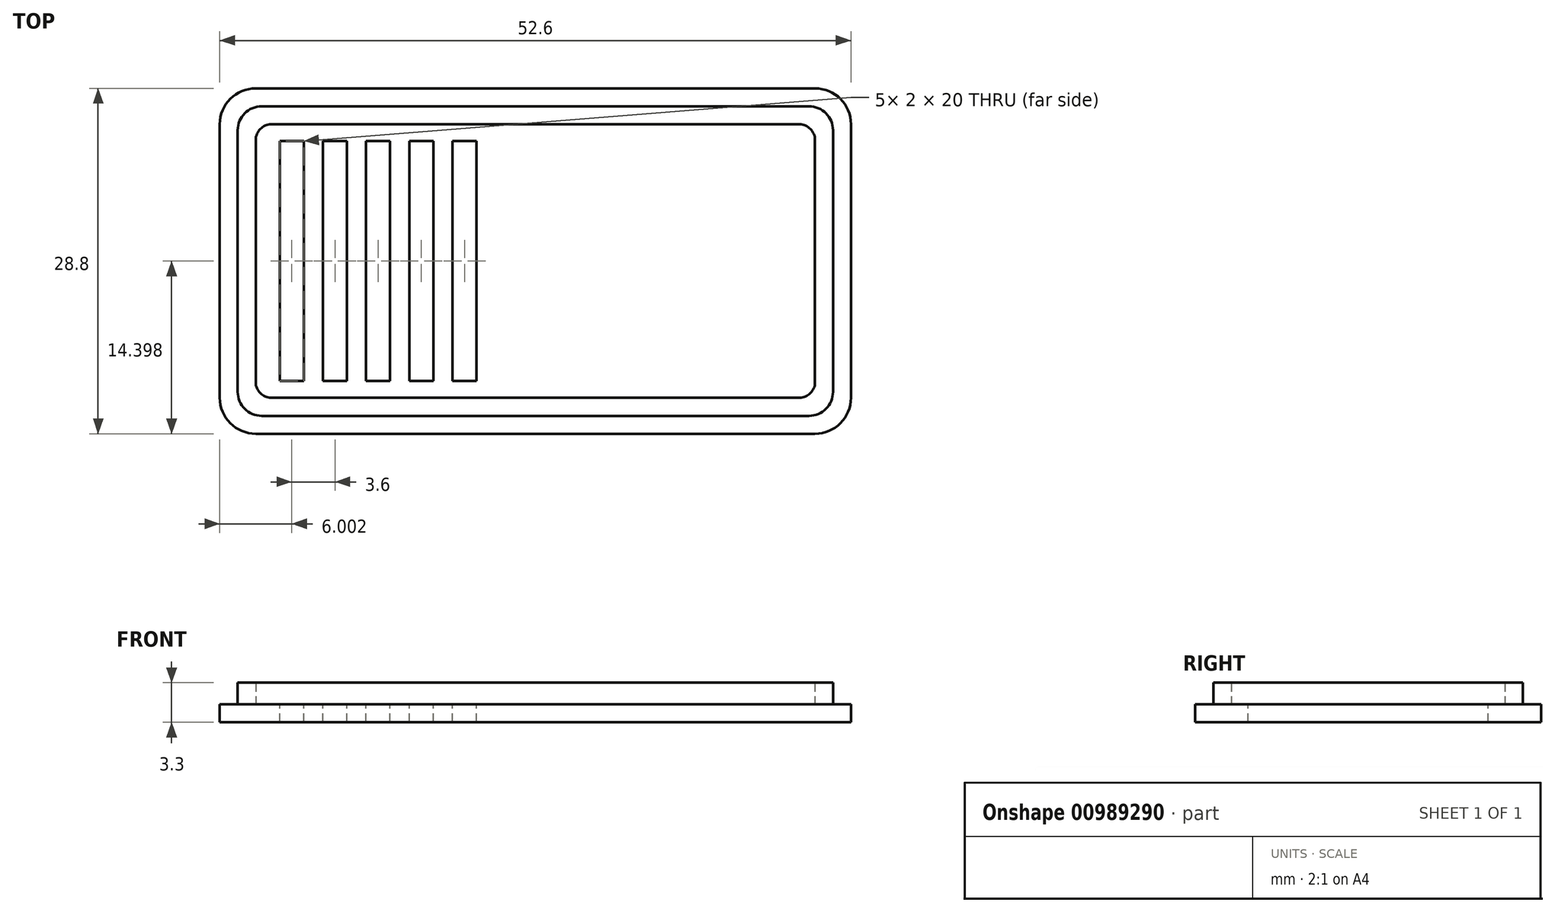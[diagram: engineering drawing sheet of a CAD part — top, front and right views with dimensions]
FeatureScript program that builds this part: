
annotation { "Feature Type Name" : "Feature", "Feature Type Description" : "" }
export const myFeature = defineFeature(function(context is Context, id is Id, definition is map)
    precondition{}
    {
        {
            var Q0;
            Q0=qCreatedBy(makeId("Top.planeOp"),FACE);
            var sketch = newSketch(context, id + "F0", { "sketchPlane" : qUnion([Q0])});
            skLineSegment(sketch, "E0.bottom", {"start": v(-22.7, 18.22) * mm, "end": v(29.9, 18.22) * mm});
            skLineSegment(sketch, "E0.top", {"start": v(-22.7, -10.58) * mm, "end": v(29.9, -10.58) * mm});
            skLineSegment(sketch, "E0.left", {"start": v(-22.7, 18.22) * mm, "end": v(-22.7, -10.58) * mm});
            skLineSegment(sketch, "E0.right", {"start": v(29.9, 18.22) * mm, "end": v(29.9, -10.58) * mm});
            skLineSegment(sketch, "E1.1", {"start": v(28.4, 16.72) * mm, "end": v(28.4, -9.08) * mm});
            skLineSegment(sketch, "E2", {"start": v(-21.2, 16.72) * mm, "end": v(-21.2, -9.08) * mm});
            skLineSegment(sketch, "E3", {"start": v(-21.2, 16.72) * mm, "end": v(28.4, 16.72) * mm});
            skLineSegment(sketch, "E4", {"start": v(-21.2, -9.08) * mm, "end": v(28.4, -9.08) * mm});
            skLineSegment(sketch, "E5.0", {"start": v(-19.7, 15.22) * mm, "end": v(26.9, 15.22) * mm});
            skLineSegment(sketch, "E5.1", {"start": v(-19.7, 15.22) * mm, "end": v(-19.7, -7.58) * mm});
            skLineSegment(sketch, "E5.2", {"start": v(-19.7, -7.58) * mm, "end": v(26.9, -7.58) * mm});
            skLineSegment(sketch, "E5.3", {"start": v(26.9, 15.22) * mm, "end": v(26.9, -7.58) * mm});
            skLineSegment(sketch, "E6", {"start": v(-19.7, 3.82) * mm, "end": v(24.51, 3.82) * mm, "construction": true});
            skLineSegment(sketch, "E7.bottom", {"start": v(-15.7, -6.18) * mm, "end": v(-17.7, -6.18) * mm});
            skLineSegment(sketch, "E7.top", {"start": v(-15.7, 13.82) * mm, "end": v(-17.7, 13.82) * mm});
            skLineSegment(sketch, "E7.left", {"start": v(-15.7, -6.18) * mm, "end": v(-15.7, 13.82) * mm});
            skLineSegment(sketch, "E7.right", {"start": v(-17.7, -6.18) * mm, "end": v(-17.7, 13.82) * mm});
            skPoint(sketch, "E7.middle", {"position": v(-16.7, 3.82) * mm});
            skLineSegment(sketch, "E8.1.0.0", {"start": v(-12.1, -6.18) * mm, "end": v(-12.1, 13.82) * mm});
            skLineSegment(sketch, "E8.1.0.1", {"start": v(-14.1, -6.18) * mm, "end": v(-14.1, 13.82) * mm});
            skLineSegment(sketch, "E8.1.0.2", {"start": v(-12.1, 13.82) * mm, "end": v(-14.1, 13.82) * mm});
            skLineSegment(sketch, "E8.1.0.3", {"start": v(-12.1, -6.18) * mm, "end": v(-14.1, -6.18) * mm});
            skLineSegment(sketch, "E8.2.0.0", {"start": v(-8.5, -6.18) * mm, "end": v(-8.5, 13.82) * mm});
            skLineSegment(sketch, "E8.2.0.1", {"start": v(-10.5, -6.18) * mm, "end": v(-10.5, 13.82) * mm});
            skLineSegment(sketch, "E8.2.0.2", {"start": v(-8.5, 13.82) * mm, "end": v(-10.5, 13.82) * mm});
            skLineSegment(sketch, "E8.2.0.3", {"start": v(-8.5, -6.18) * mm, "end": v(-10.5, -6.18) * mm});
            skLineSegment(sketch, "E8.3.0.0", {"start": v(-4.9, -6.18) * mm, "end": v(-4.9, 13.82) * mm});
            skLineSegment(sketch, "E8.3.0.1", {"start": v(-6.9, -6.18) * mm, "end": v(-6.9, 13.82) * mm});
            skLineSegment(sketch, "E8.3.0.2", {"start": v(-4.9, 13.82) * mm, "end": v(-6.9, 13.82) * mm});
            skLineSegment(sketch, "E8.3.0.3", {"start": v(-4.9, -6.18) * mm, "end": v(-6.9, -6.18) * mm});
            skLineSegment(sketch, "E8.4.0.0", {"start": v(-1.3, -6.18) * mm, "end": v(-1.3, 13.82) * mm});
            skLineSegment(sketch, "E8.4.0.1", {"start": v(-3.3, -6.18) * mm, "end": v(-3.3, 13.82) * mm});
            skLineSegment(sketch, "E8.4.0.2", {"start": v(-1.3, 13.82) * mm, "end": v(-3.3, 13.82) * mm});
            skLineSegment(sketch, "E8.4.0.3", {"start": v(-1.3, -6.18) * mm, "end": v(-3.3, -6.18) * mm});
            skLineSegment(sketch, "E8.direction1", {"start": v(-17.7, -6.18) * mm, "end": v(-14.1, -6.18) * mm, "construction": true});
            skSolve(sketch);
        }
        {
            var Q0;
            {var subQ5=sQuery(id+"F0.wireOp",EDGE,"E2");Q0=makeQuery(id+"F0.imprint","IMPRINT",FACE,{"disambiguationData":[TD([[makeQuery(id+"F0.imprint","IMPRINT",EDGE,{"derivedFrom":subQ5}),-1.0]])]});}
            var Q1;
            {var subQ4=sQuery(id+"F0.wireOp",EDGE,"E0.bottom");Q1=makeQuery(id+"F0.imprint","IMPRINT",FACE,{"disambiguationData":[TD([[makeQuery(id+"F0.imprint","IMPRINT",EDGE,{"derivedFrom":subQ4}),-1.0]])]});}
            var Q2;
            {var subQ0=sQuery(id+"F0.wireOp",EDGE,"E1.1");Q2=makeQuery(id+"F0.imprint","IMPRINT",FACE,{"disambiguationData":[TD([[makeQuery(id+"F0.imprint","IMPRINT",EDGE,{"derivedFrom":subQ0}),-1.0]])]});}
            var Q3;
            Q3=makeQuery(id+"F0.imprint","IMPRINT",FACE,{"disambiguationData":[TD([[makeQuery(id+"F0.imprint","IMPRINT",EDGE,{"derivedFrom":sQuery(id+"F0.wireOp",EDGE,"E5.0")}),-1.0]])]});
            extrude(context, id + "F1", {"entities" : qUnion([Q0, Q1, Q2, Q3]), "oppositeDirection" : true, "depth" : 1.5 * mm, "offsetDistance" : 25 * mm});
        }
        {
            var Q0;
            Q0=makeQuery(id+"F1.opExtrude","SWEPT_EDGE",EDGE,{"disambiguationData":[OSD([sQuery(id+"F0.wireOp",EDGE,"E0.bottom"),sQuery(id+"F0.wireOp",EDGE,"E0.left")])]});
            var Q1;
            Q1=makeQuery(id+"F1.opExtrude","SWEPT_EDGE",EDGE,{"disambiguationData":[OSD([sQuery(id+"F0.wireOp",EDGE,"E0.bottom"),sQuery(id+"F0.wireOp",EDGE,"E0.right")])]});
            var Q2;
            Q2=makeQuery(id+"F1.opExtrude","SWEPT_EDGE",EDGE,{"disambiguationData":[OSD([sQuery(id+"F0.wireOp",EDGE,"E0.top"),sQuery(id+"F0.wireOp",EDGE,"E0.right")])]});
            var Q3;
            Q3=makeQuery(id+"F1.opExtrude","SWEPT_EDGE",EDGE,{"disambiguationData":[OSD([sQuery(id+"F0.wireOp",EDGE,"E0.top"),sQuery(id+"F0.wireOp",EDGE,"E0.left")])]});
            fillet(context, id + "F2", {"entities" : qUnion([Q0, Q1, Q2, Q3]), "radius" : 3 * mm, "tangentPropagation" : true, "allowEdgeOverflow" : false});
        }
        {
            var Q0;
            Q0=makeQuery(id+"F0.imprint","IMPRINT",FACE,{"disambiguationData":[TD([[makeQuery(id+"F0.imprint","IMPRINT",EDGE,{"derivedFrom":sQuery(id+"F0.wireOp",EDGE,"E1.1")}),-1.0]])]});
            extrude(context, id + "F3", {"entities" : qUnion([Q0]), "operationType" : NewBodyOperationType.ADD, "depth" : 1.8 * mm, "offsetDistance" : 25 * mm});
        }
        {
            var Q0;
            Q0=makeQuery(id+"F3.opExtrude","SWEPT_EDGE",EDGE,{"disambiguationData":[OSD([sQuery(id+"F0.wireOp",EDGE,"E2"),sQuery(id+"F0.wireOp",EDGE,"E4")])]});
            var Q1;
            Q1=makeQuery(id+"F3.opExtrude","SWEPT_EDGE",EDGE,{"disambiguationData":[OSD([sQuery(id+"F0.wireOp",EDGE,"E2"),sQuery(id+"F0.wireOp",EDGE,"E3")])]});
            var Q2;
            Q2=makeQuery(id+"F3.opExtrude","SWEPT_EDGE",EDGE,{"disambiguationData":[OSD([sQuery(id+"F0.wireOp",EDGE,"E1.1"),sQuery(id+"F0.wireOp",EDGE,"E3")])]});
            var Q3;
            Q3=makeQuery(id+"F3.opExtrude","SWEPT_EDGE",EDGE,{"disambiguationData":[OSD([sQuery(id+"F0.wireOp",EDGE,"E1.1"),sQuery(id+"F0.wireOp",EDGE,"E4")])]});
            fillet(context, id + "F4", {"entities" : qUnion([Q0, Q1, Q2, Q3]), "radius" : 2 * mm, "tangentPropagation" : true, "allowEdgeOverflow" : false});
        }
        {
            var Q0;
            Q0=makeQuery(id+"F3.opExtrude","SWEPT_EDGE",EDGE,{"disambiguationData":[OSD([sQuery(id+"F0.wireOp",EDGE,"E5.0"),sQuery(id+"F0.wireOp",EDGE,"E5.1")])]});
            var Q1;
            Q1=makeQuery(id+"F3.opExtrude","SWEPT_EDGE",EDGE,{"disambiguationData":[OSD([sQuery(id+"F0.wireOp",EDGE,"E5.1"),sQuery(id+"F0.wireOp",EDGE,"E5.2")])]});
            var Q2;
            Q2=makeQuery(id+"F3.opExtrude","SWEPT_EDGE",EDGE,{"disambiguationData":[OSD([sQuery(id+"F0.wireOp",EDGE,"E5.2"),sQuery(id+"F0.wireOp",EDGE,"E5.3")])]});
            var Q3;
            Q3=makeQuery(id+"F3.opExtrude","SWEPT_EDGE",EDGE,{"disambiguationData":[OSD([sQuery(id+"F0.wireOp",EDGE,"E5.0"),sQuery(id+"F0.wireOp",EDGE,"E5.3")])]});
            fillet(context, id + "F5", {"entities" : qUnion([Q0, Q1, Q2, Q3]), "radius" : 1.3 * mm, "tangentPropagation" : true, "allowEdgeOverflow" : false});
        }
    });
